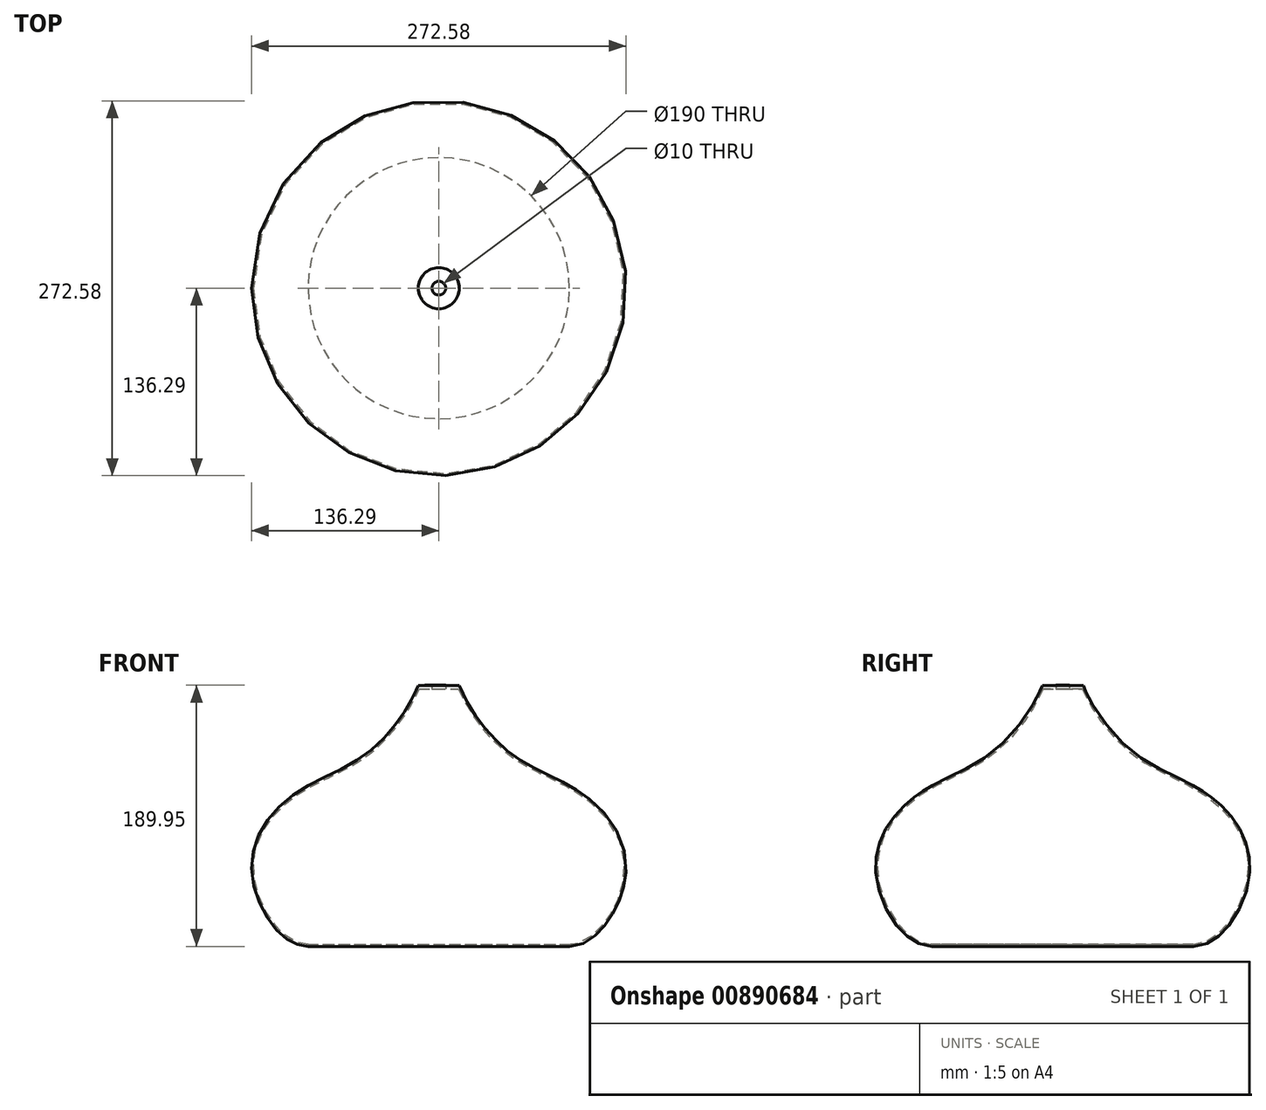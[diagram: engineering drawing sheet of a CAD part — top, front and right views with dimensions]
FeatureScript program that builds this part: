
annotation { "Feature Type Name" : "Feature", "Feature Type Description" : "" }
export const myFeature = defineFeature(function(context is Context, id is Id, definition is map)
    precondition{}
    {
        {
            var Q0;
            Q0=qCreatedBy(makeId("Front.planeOp"),FACE);
            var sketch = newSketch(context, id + "F0", { "sketchPlane" : qUnion([Q0])});
            skLineSegment(sketch, "E0", {"start": v(0, 0) * mm, "end": v(0, 190) * mm, "construction": true});
            skFitSpline(sketch, "E1", {"points": [v(95, 0) * mm, v(118.77, 12.8) * mm, v(136.15, 61.77) * mm, v(107.73, 108.75) * mm, v(54.03, 139.16) * mm, v(20.86, 177.44) * mm, v(14.93, 189.86) * mm, v(14.93, 190.16) * mm], "startDerivative": vector(180.22, 0) * mm, "endDerivative": vector(5.19, 34.48) * mm});
            skLineSegment(sketch, "E2", {"start": v(14.93, 189.86) * mm, "end": v(0, 190) * mm});
            skLineSegment(sketch, "E3", {"start": v(0, 190) * mm, "end": v(0, 187.26) * mm});
            skFitSpline(sketch, "E4.0", {"points": [v(95, 1.5) * mm, v(96.75, 1.5) * mm, v(100.3, 1.95) * mm, v(105.7, 3.99) * mm, v(110.2, 6.82) * mm, v(113.73, 9.76) * mm, v(116.34, 12.3) * mm, v(118.88, 15.18) * mm, v(122.16, 19.44) * mm, v(125.97, 25.48) * mm, v(129.85, 33.58) * mm, v(132.8, 42.25) * mm, v(134.3, 49.74) * mm, v(134.8, 55.74) * mm, v(134.8, 60.2) * mm, v(134.42, 64.62) * mm, v(133.37, 70.42) * mm, v(131.14, 77.48) * mm, v(127.12, 85.56) * mm, v(121.93, 93.14) * mm, v(116.77, 98.94) * mm, v(112.22, 103.21) * mm, v(108.62, 106.23) * mm, v(104.86, 109.03) * mm, v(99.64, 112.5) * mm, v(92.79, 116.46) * mm, v(84.23, 120.81) * mm, v(75.53, 125.04) * mm, v(68.33, 128.69) * mm, v(62.69, 131.8) * mm, v(58.54, 134.28) * mm, v(54.5, 136.93) * mm, v(50.61, 139.78) * mm, v(46.89, 142.83) * mm, v(42.14, 147.1) * mm, v(36.64, 152.73) * mm, v(30.76, 159.74) * mm, v(26.49, 165.6) * mm, v(23.47, 170.15) * mm, v(21.4, 173.48) * mm, v(19.55, 176.7) * mm, v(17.9, 179.75) * mm, v(16.72, 182.09) * mm, v(15.9, 183.79) * mm, v(15.36, 184.97) * mm, v(14.87, 186.03) * mm, v(14.46, 186.98) * mm, v(14.17, 187.66) * mm, v(13.98, 188.13) * mm, v(13.85, 188.45) * mm, v(13.74, 188.73) * mm, v(13.65, 188.98) * mm, v(13.57, 189.19) * mm, v(13.52, 189.34) * mm, v(13.49, 189.46) * mm, v(13.46, 189.57) * mm, v(13.42, 189.74) * mm, v(13.4, 189.95) * mm, v(13.41, 190.14) * mm, v(13.43, 190.26) * mm, v(13.44, 190.33) * mm, v(13.44, 190.37) * mm, v(13.45, 190.39) * mm]});
            skLineSegment(sketch, "E5", {"start": v(95, 1.5) * mm, "end": v(95, 0) * mm});
            skLineSegment(sketch, "E6", {"start": v(0, 187.26) * mm, "end": v(14.34, 187.26) * mm});
            skSolve(sketch);
        }
        {
            var Q0;
            {var subQ0=sQuery(id+"F0.wireOp",EDGE,"E3");Q0=makeQuery(id+"F0.imprint","IMPRINT",FACE,{"disambiguationData":[TD([[makeQuery(id+"F0.imprint","IMPRINT",EDGE,{"derivedFrom":subQ0}),1.0]])]});}
            var Q1;
            {var subQ0=sQuery(id+"F0.wireOp",EDGE,"E5");Q1=makeQuery(id+"F0.imprint","IMPRINT",FACE,{"disambiguationData":[TD([[makeQuery(id+"F0.imprint","IMPRINT",EDGE,{"derivedFrom":subQ0}),1.0]])]});}
            var Q2;
            Q2=sQuery(id+"F0.wireOp",EDGE,"E0");
            revolve(context, id + "F1", {"surfaceOperationType" : NewSurfaceOperationType.NEW, "entities" : qUnion([Q0, Q1]), "axis" : qUnion([Q2]), "revolveType" : RevolveType.FULL});
        }
        {
            var Q0;
            Q0=qCreatedBy(makeId("Top.planeOp"),FACE);
            var sketch = newSketch(context, id + "F2", { "sketchPlane" : qUnion([Q0])});
            skCircle(sketch, "E7", {"center": v(0, 0) * mm, "radius": 5 * mm});
            skSolve(sketch);
        }
        {
            var Q0;
            Q0 = qSketchRegion(id + "F2", true);
            extrude(context, id + "F3", {"entities" : qUnion([Q0]), "operationType" : NewBodyOperationType.REMOVE, "depth" : 190 * mm, "offsetDistance" : 25 * mm});
        }
    });
